# Revit family: Thorn VOYAGER SQUARE
name_source: partatom
category: Lighting Fixtures
revit_build: Autodesk Revit 2016 (Build: 20150220_1215(x64)
units: mm (PartAtom-declared; Revit-internal decimal feet)

## family parameters
Cut with Voids When Loaded = No
Host = Face
Light Source = Yes
OmniClass Number = 23.80.70.11
OmniClass Title = Luminaries for Internal Lighting
Part Type = Normal
Room Calculation Point = No
Round Connector Dimension = Use Diameter
Shared = No

## types (4) — shared parameters
Apparent Load = 5 VA
Assembly Code = D5020200
Body = ZG_Metal_White
Color Filter = 16777215
Description = Square wall mounted LED safety sign luminaire
Dimming Lamp Color Temperature Shift = <None>
Emit Shape Visible in Rendering = No
Emit from Rectangle Length = 211 mm  [stored 0.692257 ft]
Emit from Rectangle Width = 211 mm  [stored 0.692257 ft]
Height = 58 mm
Lamp = LED
Length = 277 mm
Manufacturer = Thorn Lighting
Photometric Web File = TLG_SP_0043592.IES
Tilt Angle = -90.00°
Voltage = 230 V
Width = 277 mm
zero-valued in all types: Default Elevation

## per-type parameters (varying)
| type | Escape Down | Escape Left | Escape Right | Escape Up | Model | URL |
| Voyager Square 220 P MSW E1D WH SP1-E001-L | No | Yes | No | No | 96631331 | www.thornlighting.com/96631331 |
| Voyager Square 220 P MSW E1D WH SP1-E002-D | Yes | No | No | No | 96635064 | www.thornlighting.com/96635064 |
| Voyager Square 220 P MSW E1D WH SP1-E002-R | No | No | Yes | No | 96635037 | www.thornlighting.com/96635037 |
| Voyager Square 220 P MSW E1D WH SP1-E002-UP | No | No | No | Yes | 96635067 | www.thornlighting.com/96635067 |

note: [stored X ft] marks values corroborated as IEEE doubles in the binary element streams (Revit-internal decimal feet)

## geometry (parser evidence)
native form markers: Sweep x3
no freeform markers — native parametric forms only
